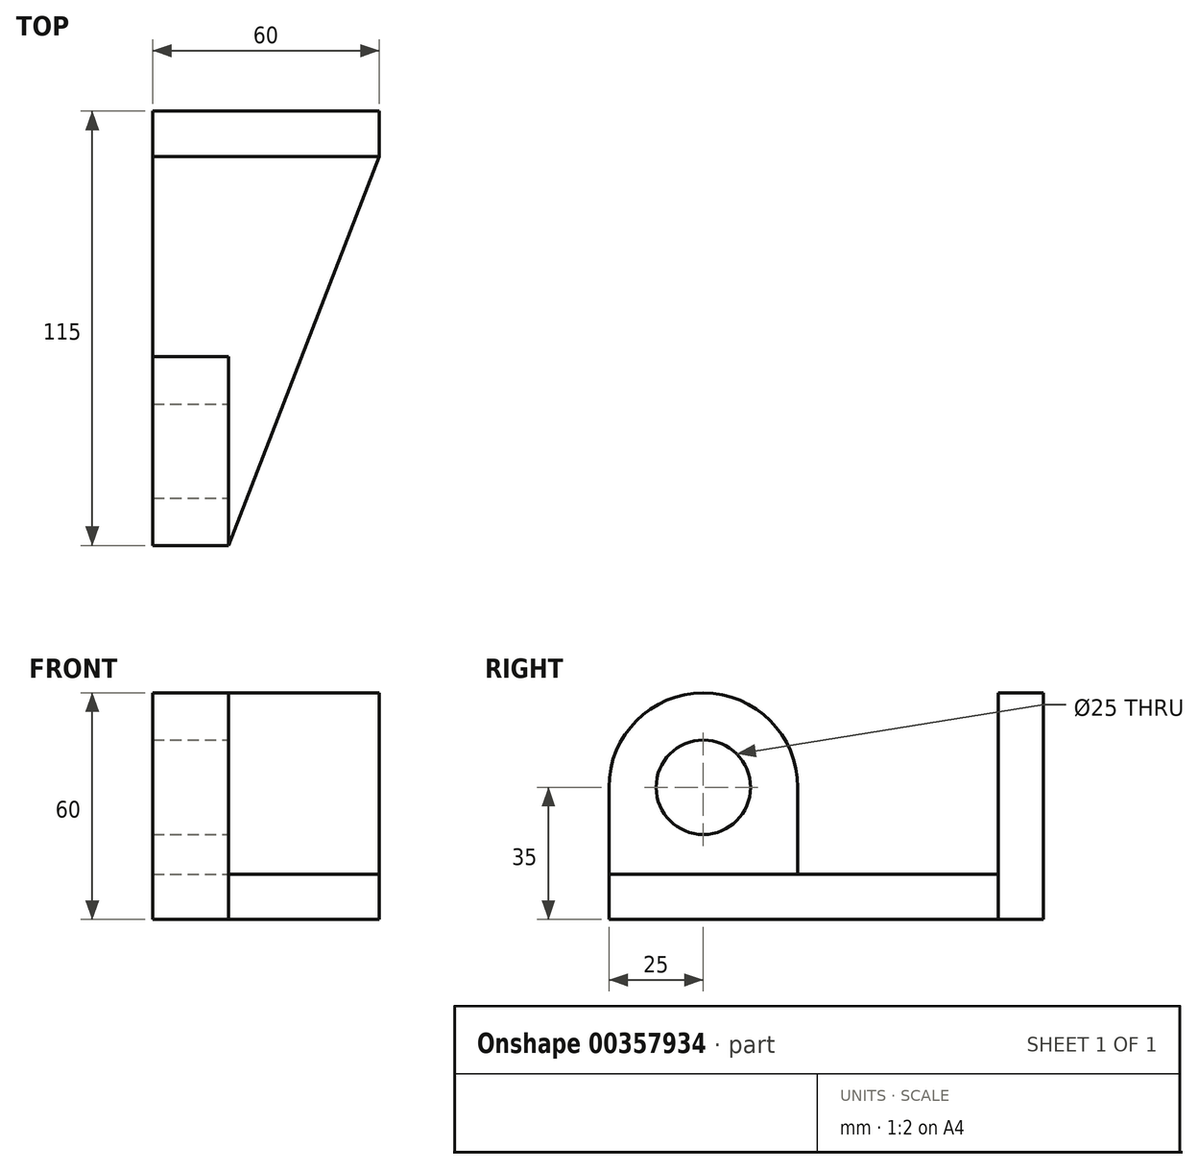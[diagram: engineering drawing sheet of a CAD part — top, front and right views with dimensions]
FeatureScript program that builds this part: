
annotation { "Feature Type Name" : "Feature", "Feature Type Description" : "" }
export const myFeature = defineFeature(function(context is Context, id is Id, definition is map)
    precondition{}
    {
        {
            var Q0;
            Q0=qCreatedBy(makeId("Top.planeOp"),FACE);
            var sketch = newSketch(context, id + "F0", { "sketchPlane" : qUnion([Q0])});
            skLineSegment(sketch, "E0.bottom", {"start": v(-30, 57.5) * mm, "end": v(30, 57.5) * mm});
            skLineSegment(sketch, "E0.top", {"start": v(-30, -57.5) * mm, "end": v(30, -57.5) * mm});
            skLineSegment(sketch, "E0.left", {"start": v(-30, 57.5) * mm, "end": v(-30, -57.5) * mm});
            skLineSegment(sketch, "E0.right", {"start": v(30, 57.5) * mm, "end": v(30, -57.5) * mm});
            skPoint(sketch, "E0.middle", {"position": v(0, 0) * mm});
            skSolve(sketch);
        }
        {
            var Q0;
            Q0 = qSketchRegion(id + "F0", true);
            extrude(context, id + "F1", {"entities" : qUnion([Q0]), "depth" : 12 * mm});
        }
        {
            var Q0;
            Q0=makeQuery(id+"F1.opExtrude","CAP_FACE",FACE,{"disambiguationData":[OSD([sQuery(id+"F0.wireOp",EDGE,"E0.bottom"),sQuery(id+"F0.wireOp",EDGE,"E0.top"),sQuery(id+"F0.wireOp",EDGE,"E0.left"),sQuery(id+"F0.wireOp",EDGE,"E0.right")])],"isStart":false});
            var sketch = newSketch(context, id + "F2", { "sketchPlane" : qUnion([Q0])});
            skLineSegment(sketch, "E1.bottom", {"start": v(-30, 57.5) * mm, "end": v(30, 57.5) * mm});
            skLineSegment(sketch, "E1.top", {"start": v(-30, 45.5) * mm, "end": v(30, 45.5) * mm});
            skLineSegment(sketch, "E1.left", {"start": v(-30, 57.5) * mm, "end": v(-30, 45.5) * mm});
            skLineSegment(sketch, "E1.right", {"start": v(30, 57.5) * mm, "end": v(30, 45.5) * mm});
            skSolve(sketch);
        }
        {
            var Q0;
            Q0 = qSketchRegion(id + "F2", true);
            extrude(context, id + "F3", {"entities" : qUnion([Q0]), "operationType" : NewBodyOperationType.ADD, "depth" : 48 * mm});
        }
        {
            var Q0;
            Q0=makeQuery(id+"F1.opExtrude","CAP_FACE",FACE,{"disambiguationData":[OSD([sQuery(id+"F0.wireOp",EDGE,"E0.bottom"),sQuery(id+"F0.wireOp",EDGE,"E0.top"),sQuery(id+"F0.wireOp",EDGE,"E0.left"),sQuery(id+"F0.wireOp",EDGE,"E0.right")])],"isStart":false});
            var sketch = newSketch(context, id + "F4", { "sketchPlane" : qUnion([Q0])});
            skLineSegment(sketch, "E2.bottom", {"start": v(-30, -57.5) * mm, "end": v(-10, -57.5) * mm});
            skLineSegment(sketch, "E2.top", {"start": v(-30, -7.5) * mm, "end": v(-10, -7.5) * mm});
            skLineSegment(sketch, "E2.left", {"start": v(-30, -57.5) * mm, "end": v(-30, -7.5) * mm});
            skLineSegment(sketch, "E2.right", {"start": v(-10, -57.5) * mm, "end": v(-10, -7.5) * mm});
            skSolve(sketch);
        }
        {
            var Q0;
            Q0 = qSketchRegion(id + "F4", true);
            extrude(context, id + "F5", {"entities" : qUnion([Q0]), "operationType" : NewBodyOperationType.ADD, "depth" : 48 * mm});
        }
        {
            var Q0;
            Q0=makeQuery(id+"F5.opExtrude","SWEPT_FACE",FACE,{"disambiguationData":[OSD([sQuery(id+"F4.wireOp",EDGE,"E2.right")])]});
            var sketch = newSketch(context, id + "F6", { "sketchPlane" : qUnion([Q0])});
            skCircle(sketch, "E3", {"center": v(-32.5, 35) * mm, "radius": 12.5 * mm});
            skPoint(sketch, "E3.centerSnap0", {"position": v(-32.5, 60) * mm});
            skSolve(sketch);
        }
        {
            var Q0;
            Q0 = qSketchRegion(id + "F6", true);
            extrude(context, id + "F7", {"entities" : qUnion([Q0]), "operationType" : NewBodyOperationType.REMOVE, "endBound" : BoundingType.THROUGH_ALL, "oppositeDirection" : true, "depth" : 25 * mm});
        }
        {
            var Q0;
            Q0=makeQuery(id+"F5.opExtrude","SWEPT_FACE",FACE,{"disambiguationData":[OSD([sQuery(id+"F4.wireOp",EDGE,"E2.right")])]});
            var sketch = newSketch(context, id + "F8", { "sketchPlane" : qUnion([Q0])});
            skArc(sketch, "E4", {"start": v(-7.5, 35) * mm, "mid": v(-32.5, 60) * mm, "end": v(-57.5, 35) * mm});
            skLineSegment(sketch, "E5", {"start": v(-57.5, 35) * mm, "end": v(-57.5, 60) * mm});
            skLineSegment(sketch, "E6", {"start": v(-57.5, 60) * mm, "end": v(-7.5, 60) * mm});
            skLineSegment(sketch, "E7", {"start": v(-7.5, 60) * mm, "end": v(-7.5, 35) * mm});
            skSolve(sketch);
        }
        {
            var Q0;
            Q0 = qSketchRegion(id + "F8", true);
            extrude(context, id + "F9", {"entities" : qUnion([Q0]), "operationType" : NewBodyOperationType.REMOVE, "endBound" : BoundingType.THROUGH_ALL, "oppositeDirection" : true, "depth" : 25 * mm});
        }
        {
            var Q0;
            Q0=makeQuery(id+"F1.opExtrude","CAP_FACE",FACE,{"disambiguationData":[OSD([sQuery(id+"F0.wireOp",EDGE,"E0.bottom"),sQuery(id+"F0.wireOp",EDGE,"E0.top"),sQuery(id+"F0.wireOp",EDGE,"E0.left"),sQuery(id+"F0.wireOp",EDGE,"E0.right")])],"isStart":false});
            var sketch = newSketch(context, id + "F10", { "sketchPlane" : qUnion([Q0])});
            skLineSegment(sketch, "E8", {"start": v(-10, -57.5) * mm, "end": v(30, -57.5) * mm});
            skLineSegment(sketch, "E9", {"start": v(30, -57.5) * mm, "end": v(30, 45.5) * mm});
            skLineSegment(sketch, "E10", {"start": v(30, 45.5) * mm, "end": v(-10, -57.5) * mm});
            skSolve(sketch);
        }
        {
            var Q0;
            Q0=makeQuery(id+"F10.imprint","IMPRINT",FACE,{"disambiguationData":[TD([[makeQuery(id+"F10.imprint","IMPRINT",EDGE,{"derivedFrom":sQuery(id+"F10.wireOp",EDGE,"E8")}),1.0]])]});
            extrude(context, id + "F11", {"entities" : qUnion([Q0]), "operationType" : NewBodyOperationType.REMOVE, "endBound" : BoundingType.THROUGH_ALL, "oppositeDirection" : true, "depth" : 25 * mm});
        }
    });
